# Revit family: HB-6700CLR
name_source: partatom
category: 衛工裝置
revit_build: Autodesk Revit 2015 (Build: 20140223_1515(x64)
units: mm (PartAtom-declared; Revit-internal decimal feet)

## types (2) — shared parameters
ADA Compliant = X
Assembly Code = D2010600
Default Elevation = 0"
Finish(es) = CP, PVDPB, PVDBF
Fixture Color = Not Applicable
Fixture Material = Chrome Plated
Flush Volume(s)/Flow Rate(s) = 2.2gpm(8.25 Lpm) Vandal Resistent Spray Head
Manufacturer = Hydrotek International, Inc.
Mounting = Wall-Mount
NSF Certification = NSF/ANSI standard 372
Operation = Sensor-Activated
Price = Prices may vary. Please consult Hydrotek Int'l for most up-to-date price list.
Product URL = http://www.hydrotekintl.com
Revised Date = 07/28/2015
URL = http://www.hydrotekintl.com
Warranty = 3 Years (Limited)

## per-type parameters (varying)
| type | Description | P. Plug-in transformer | Power Source |
| HB-6700CLR | Battery Powered, Sensor Activated, Chrome Plated Brass, Electronic Faucet. | Not Applicable | Battery Powered |
| H-6700CLR | AC Powered, Sensor Activated, Chrome Plated Brass, Electronic Faucet. | Applicable | AC Powered |

note: column(s) folded — value = type name in every type: Model

## geometry (parser evidence)
native form markers: Sweep x3
no freeform markers — native parametric forms only
